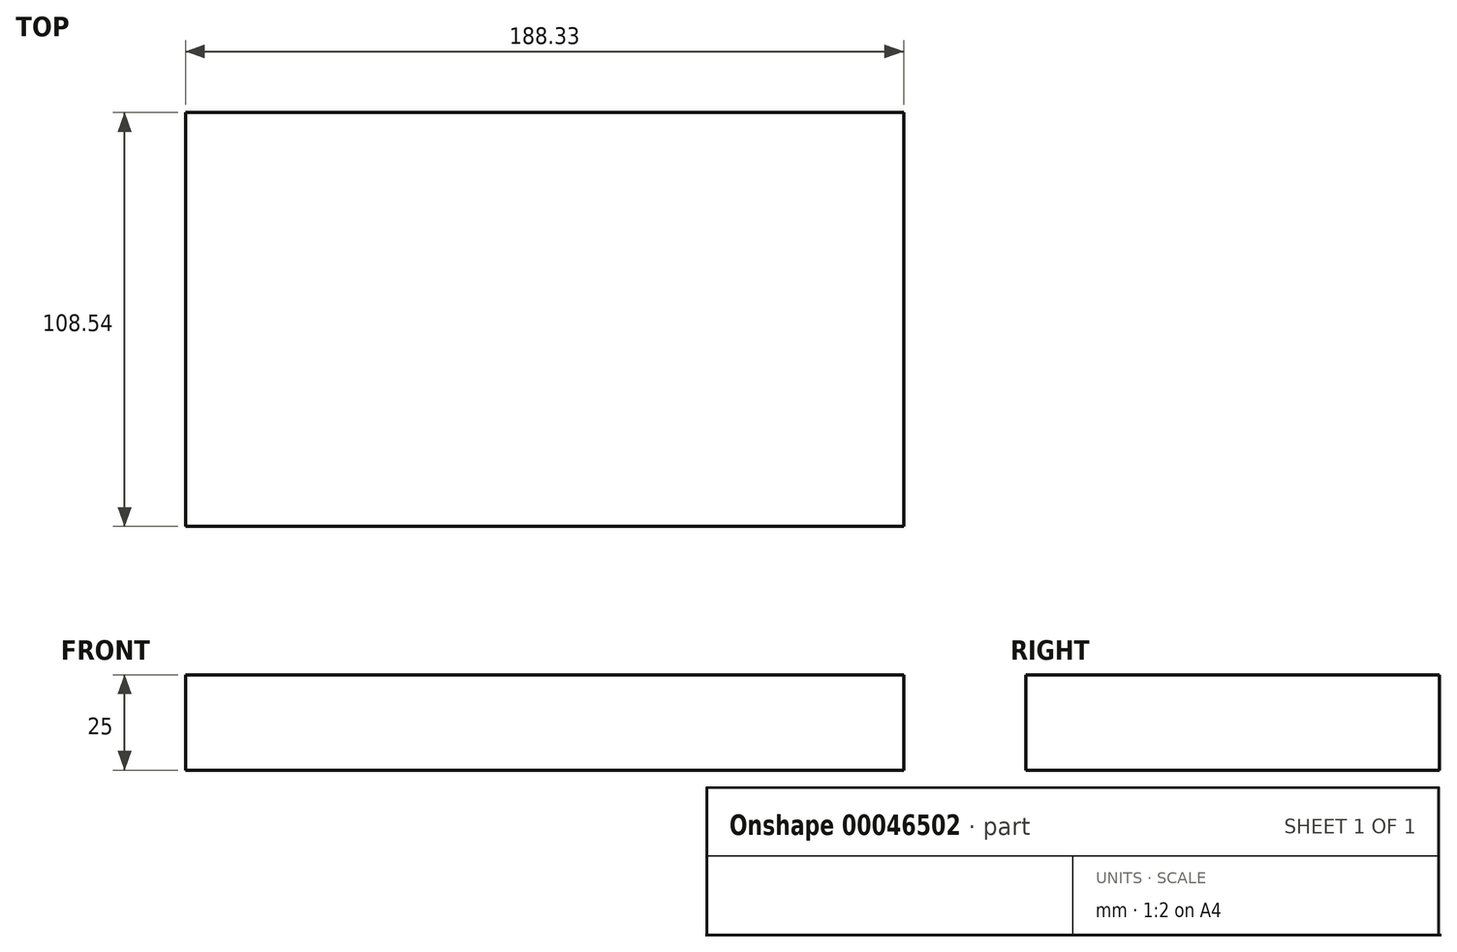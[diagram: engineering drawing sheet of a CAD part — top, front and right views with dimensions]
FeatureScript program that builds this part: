
annotation { "Feature Type Name" : "Feature", "Feature Type Description" : "" }
export const myFeature = defineFeature(function(context is Context, id is Id, definition is map)
    precondition{}
    {
        {
            var Q0;
            Q0=qCreatedBy(makeId("Top.planeOp"),FACE);
            var sketch = newSketch(context, id + "F0", { "sketchPlane" : qUnion([Q0])});
            skLineSegment(sketch, "E0.bottom", {"start": v(-66.19, 54.61) * mm, "end": v(122.14, 54.61) * mm});
            skLineSegment(sketch, "E0.top", {"start": v(-66.19, -53.93) * mm, "end": v(122.14, -53.93) * mm});
            skLineSegment(sketch, "E0.left", {"start": v(-66.19, 54.61) * mm, "end": v(-66.19, -53.93) * mm});
            skLineSegment(sketch, "E0.right", {"start": v(122.14, 54.61) * mm, "end": v(122.14, -53.93) * mm});
            skSolve(sketch);
        }
        {
            var Q0;
            Q0=makeQuery(id+"F0.imprint","IMPRINT",FACE,{"disambiguationData":[TD([[makeQuery(id+"F0.imprint","IMPRINT",EDGE,{"derivedFrom":sQuery(id+"F0.wireOp",EDGE,"E0.bottom")}),-1.0]])]});
            extrude(context, id + "F1", {"entities" : qUnion([Q0]), "oppositeDirection" : true, "depth" : 25 * mm});
        }
    });
